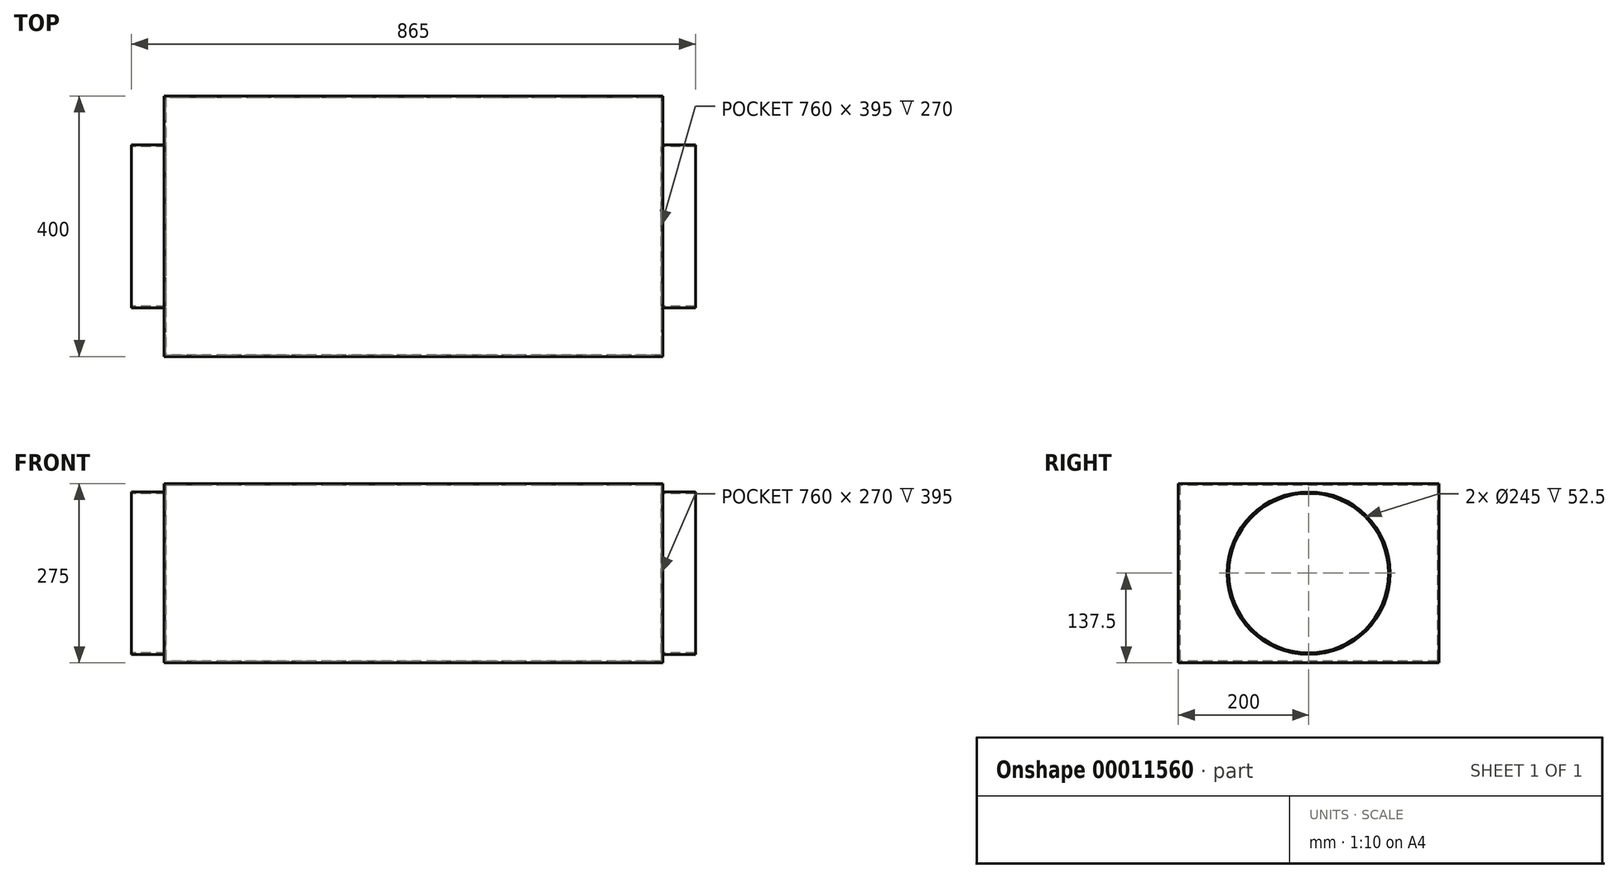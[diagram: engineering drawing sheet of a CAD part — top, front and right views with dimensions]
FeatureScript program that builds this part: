
annotation { "Feature Type Name" : "Feature", "Feature Type Description" : "" }
export const myFeature = defineFeature(function(context is Context, id is Id, definition is map)
    precondition{}
    {
        {
            var Q0;
            Q0=qCreatedBy(makeId("Right.planeOp"),FACE);
            var sketch = newSketch(context, id + "F0", { "sketchPlane" : qUnion([Q0])});
            skLineSegment(sketch, "E0.rect.bottom", {"start": v(200, 137.5) * mm, "end": v(-200, 137.5) * mm});
            skLineSegment(sketch, "E0.rect.top", {"start": v(200, -137.5) * mm, "end": v(-200, -137.5) * mm});
            skLineSegment(sketch, "E0.rect.left", {"start": v(200, 137.5) * mm, "end": v(200, -137.5) * mm});
            skLineSegment(sketch, "E0.rect.right", {"start": v(-200, 137.5) * mm, "end": v(-200, -137.5) * mm});
            skPoint(sketch, "E0.rect.middle", {"position": v(0, 0) * mm});
            skSolve(sketch);
        }
        {
            var Q0;
            Q0 = qSketchRegion(id + "F0", true);
            extrude(context, id + "F1", {"entities" : qUnion([Q0]), "endBound" : BoundingType.SYMMETRIC, "depth" : 765 * mm});
        }
        {
            var Q0;
            Q0=qCreatedBy(makeId("Right.planeOp"),FACE);
            var sketch = newSketch(context, id + "F2", { "sketchPlane" : qUnion([Q0])});
            skCircle(sketch, "E1", {"center": v(0, 0) * mm, "radius": 125 * mm});
            skSolve(sketch);
        }
        {
            var Q0;
            Q0 = qSketchRegion(id + "F2", true);
            extrude(context, id + "F3", {"entities" : qUnion([Q0]), "operationType" : NewBodyOperationType.ADD, "endBound" : BoundingType.SYMMETRIC, "depth" : 865 * mm});
        }
        {
            var Q0;
            Q0=makeQuery(id+"F3.opExtrude","CAP_FACE",FACE,{"disambiguationData":[OSD([sQuery(id+"F2.wireOp",EDGE,"E1")])],"isStart":false});
            var Q1;
            Q1=makeQuery(id+"F3.opExtrude","CAP_FACE",FACE,{"disambiguationData":[OSD([sQuery(id+"F2.wireOp",EDGE,"E1")])],"isStart":true});
            shell(context, id + "F4", {"entities" : qUnion([Q0, Q1]), "thickness" : 2.5 * mm});
        }
    });
